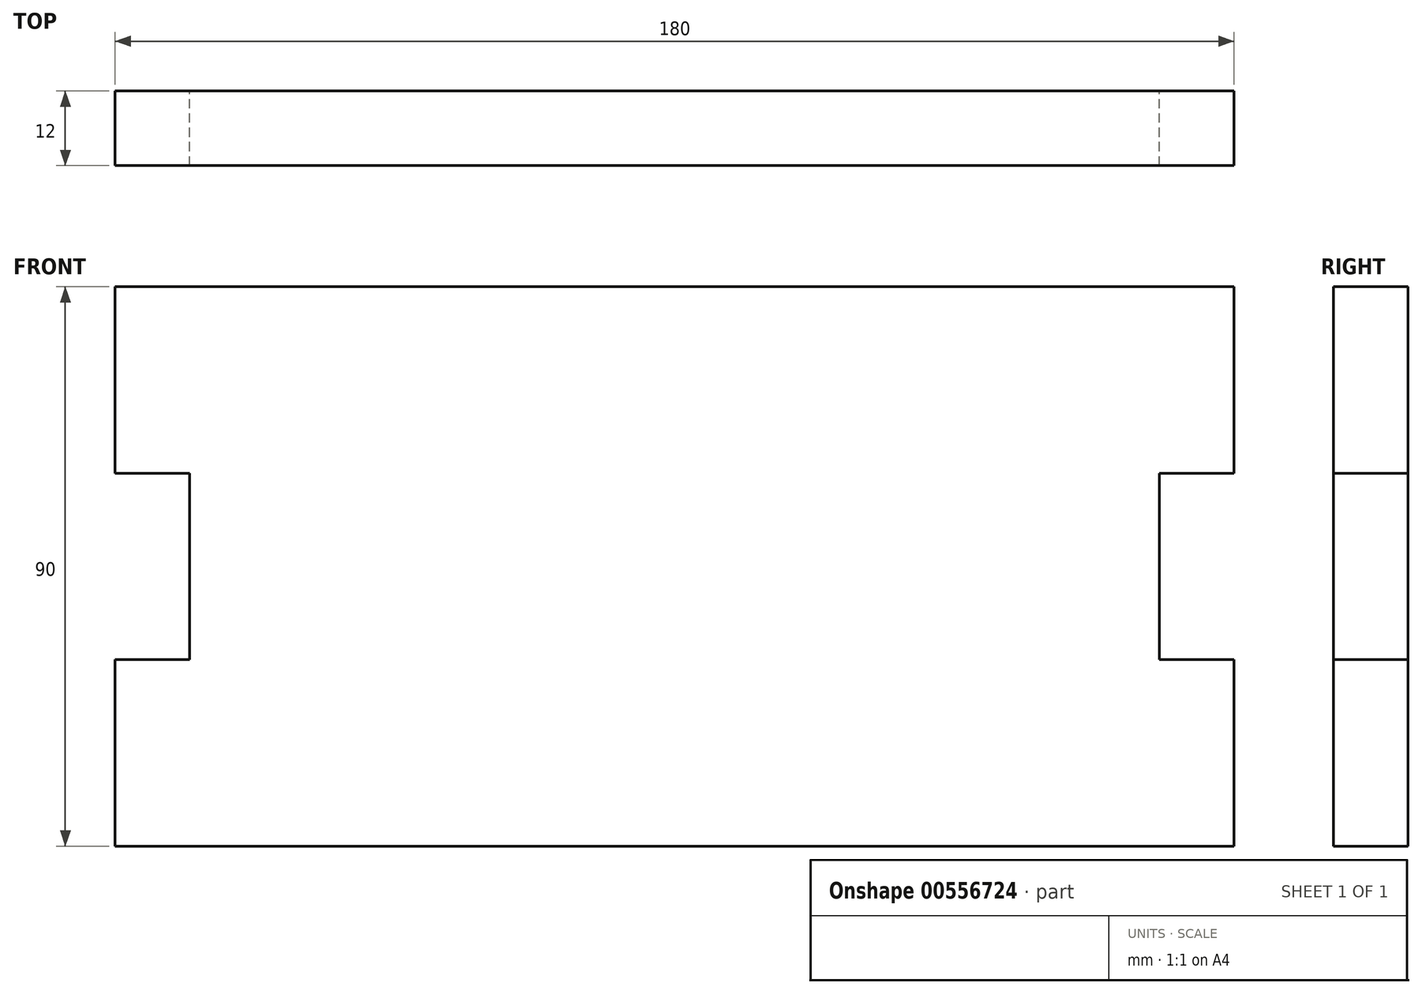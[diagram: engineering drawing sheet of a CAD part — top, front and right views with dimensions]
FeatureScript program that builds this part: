
annotation { "Feature Type Name" : "Feature", "Feature Type Description" : "" }
export const myFeature = defineFeature(function(context is Context, id is Id, definition is map)
    precondition{}
    {
        {
            var Q0;
            Q0=qCreatedBy(makeId("Front.planeOp"),FACE);
            var sketch = newSketch(context, id + "F0", { "sketchPlane" : qUnion([Q0])});
            skLineSegment(sketch, "E0", {"start": v(0, 0) * mm, "end": v(0, 30) * mm});
            skLineSegment(sketch, "E1", {"start": v(0, 30) * mm, "end": v(12, 30) * mm});
            skLineSegment(sketch, "E2", {"start": v(12, 30) * mm, "end": v(12, 60) * mm});
            skLineSegment(sketch, "E3", {"start": v(12, 60) * mm, "end": v(0, 60) * mm});
            skLineSegment(sketch, "E4", {"start": v(0, 60) * mm, "end": v(0, 90) * mm});
            skLineSegment(sketch, "E5", {"start": v(0, 90) * mm, "end": v(90, 90) * mm});
            skLineSegment(sketch, "E6", {"start": v(90, 90) * mm, "end": v(90, 0) * mm, "construction": true});
            skLineSegment(sketch, "E7", {"start": v(90, 0) * mm, "end": v(0, 0) * mm});
            skLineSegment(sketch, "E8.MirrorCS", {"start": v(180, 0) * mm, "end": v(180, 30) * mm});
            skLineSegment(sketch, "E9.MirrorCS", {"start": v(168, 60) * mm, "end": v(180, 60) * mm});
            skLineSegment(sketch, "E10.MirrorCS", {"start": v(168, 30) * mm, "end": v(168, 60) * mm});
            skLineSegment(sketch, "E11.MirrorCS", {"start": v(180, 60) * mm, "end": v(180, 90) * mm});
            skLineSegment(sketch, "E12.MirrorCS", {"start": v(90, 0) * mm, "end": v(180, 0) * mm});
            skLineSegment(sketch, "E13.MirrorCS", {"start": v(180, 90) * mm, "end": v(90, 90) * mm});
            skLineSegment(sketch, "E14.MirrorCS", {"start": v(180, 30) * mm, "end": v(168, 30) * mm});
            skSolve(sketch);
        }
        {
            var Q0;
            Q0=makeQuery(id+"F0.imprint","IMPRINT",FACE,{"disambiguationData":[TD([[makeQuery(id+"F0.imprint","IMPRINT",EDGE,{"derivedFrom":sQuery(id+"F0.wireOp",EDGE,"E0")}),-1.0]])]});
            extrude(context, id + "F1", {"entities" : qUnion([Q0]), "endBound" : BoundingType.SYMMETRIC, "depth" : 12 * mm, "offsetDistance" : 25 * mm});
        }
    });
